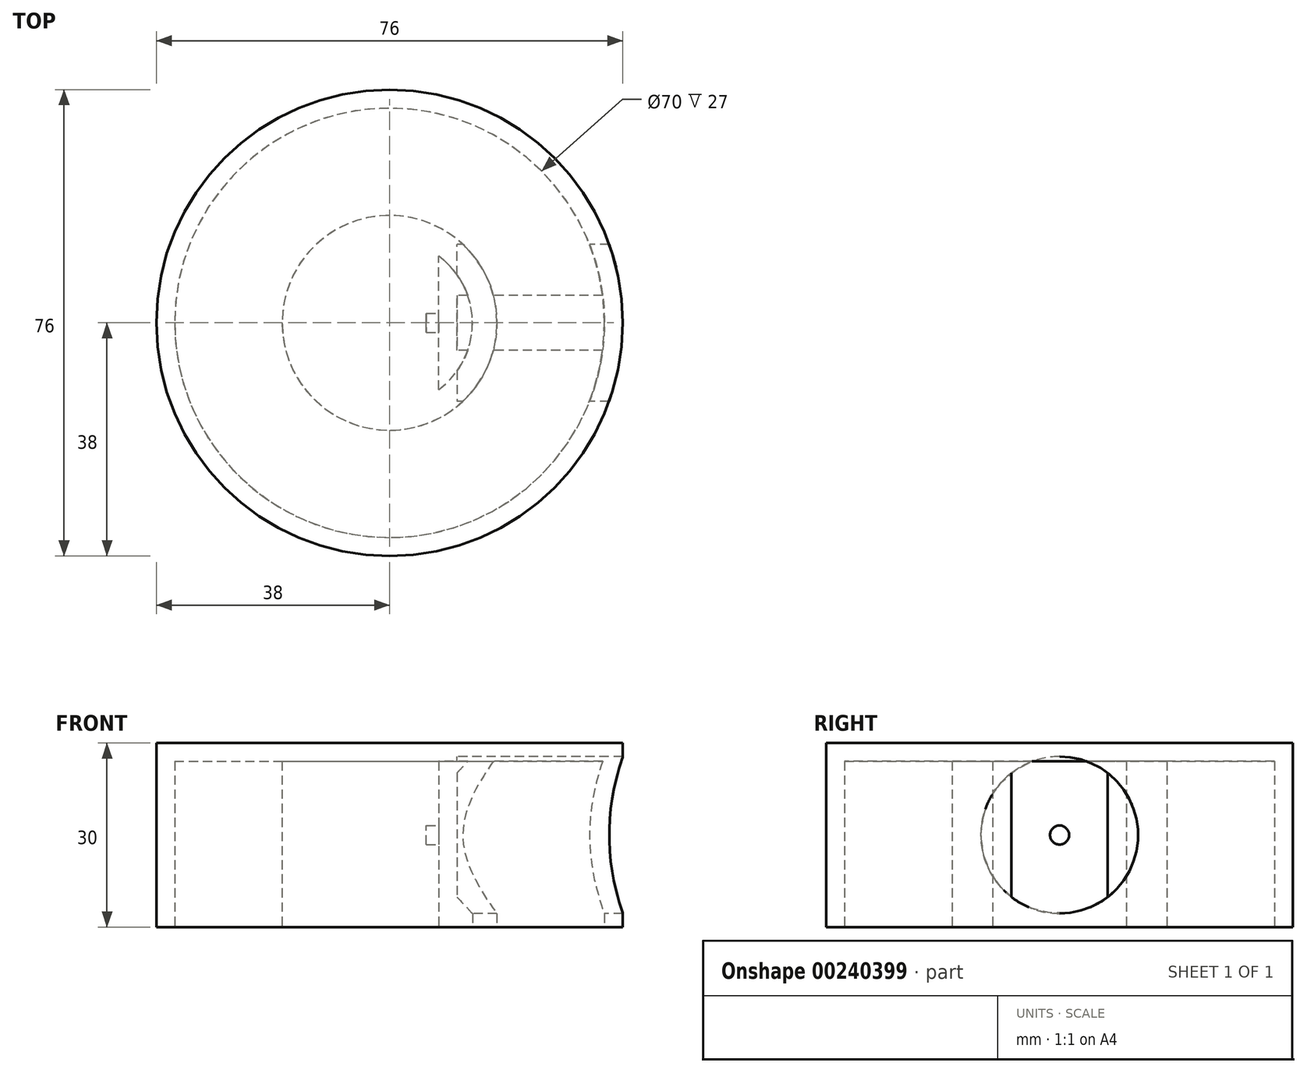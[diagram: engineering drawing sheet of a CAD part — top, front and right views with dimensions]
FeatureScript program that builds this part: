
annotation { "Feature Type Name" : "Feature", "Feature Type Description" : "" }
export const myFeature = defineFeature(function(context is Context, id is Id, definition is map)
    precondition{}
    {
        {
            var Q0;
            Q0=qCreatedBy(makeId("Top.planeOp"),FACE);
            var sketch = newSketch(context, id + "F0", { "sketchPlane" : qUnion([Q0])});
            skCircle(sketch, "E0", {"center": v(0, 0) * mm, "radius": 38 * mm});
            skSolve(sketch);
        }
        {
            var Q0;
            Q0 = qSketchRegion(id + "F0", true);
            extrude(context, id + "F1", {"entities" : qUnion([Q0]), "depth" : 30 * mm});
        }
        {
            var Q0;
            Q0=makeQuery(id+"F1.opExtrude","CAP_FACE",FACE,{"disambiguationData":[OSD([sQuery(id+"F0.wireOp",EDGE,"E0")])],"isStart":true});
            var sketch = newSketch(context, id + "F2", { "sketchPlane" : qUnion([Q0])});
            skCircle(sketch, "E1", {"center": v(0, 0) * mm, "radius": 17.5 * mm});
            skCircle(sketch, "E2", {"center": v(0, 0) * mm, "radius": 35 * mm});
            skSolve(sketch);
        }
        {
            var Q0;
            Q0 = qSketchRegion(id + "F2", true);
            extrude(context, id + "F3", {"entities" : qUnion([Q0]), "operationType" : NewBodyOperationType.REMOVE, "oppositeDirection" : true, "depth" : 27 * mm});
        }
        {
            var Q0;
            Q0=qCreatedBy(makeId("Right.planeOp"),FACE);
            var sketch = newSketch(context, id + "F4", { "sketchPlane" : qUnion([Q0])});
            skCircle(sketch, "E3", {"center": v(0, 15) * mm, "radius": 12.8 * mm});
            skSolve(sketch);
        }
        {
            var Q0;
            Q0 = qSketchRegion(id + "F4", true);
            extrude(context, id + "F5", {"entities" : qUnion([Q0]), "operationType" : NewBodyOperationType.REMOVE, "depth" : 46 * mm, "hasSecondDirection" : true, "secondDirectionOppositeDirection" : false, "secondDirectionDepth" : 11 * mm});
        }
        {
            var Q0;
            Q0=makeQuery(id+"F3.boolean.opBoolean","SPLIT",FACE,{"disambiguationData":[TD([makeQuery(id+"F3.opExtrude","SWEPT_FACE",FACE,{"disambiguationData":[OSD([sQuery(id+"F2.wireOp",EDGE,"E1")])]})])],"derivedFrom":makeQuery(id+"F1.opExtrude","CAP_FACE",FACE,{"disambiguationData":[OSD([sQuery(id+"F0.wireOp",EDGE,"E0")])],"isStart":true})});
            var sketch = newSketch(context, id + "F6", { "sketchPlane" : qUnion([Q0])});
            skCircle(sketch, "E4.0", {"center": v(0, 0) * mm, "radius": 13.5 * mm});
            skLineSegment(sketch, "E5.0", {"start": v(8, 12.8) * mm, "end": v(8, -12.8) * mm});
            skSolve(sketch);
        }
        {
            var Q0;
            {var subQ0=sQuery(id+"F6.wireOp",EDGE,"E5.0");var subQ1=sQuery(id+"F6.wireOp",EDGE,"E4.0");var subQ2=makeQuery(id+"F6.imprint","INTERSECT",VERTEX,{"disambiguationData":[OD(0.0)],"derivedFrom":[subQ1,subQ0]});Q0=makeQuery(id+"F6.imprint","IMPRINT",FACE,{"disambiguationData":[TD([[makeQuery(id+"F6.imprint","IMPRINT",EDGE,{"disambiguationData":[TD([[subQ2,-1.0]])],"derivedFrom":subQ1}),1.0]])]});}
            extrude(context, id + "F7", {"entities" : qUnion([Q0]), "operationType" : NewBodyOperationType.REMOVE, "oppositeDirection" : true, "depth" : 27 * mm});
        }
        {
            var Q0;
            Q0=makeQuery(id+"F5.boolean.opBoolean","COPY",FACE,{"derivedFrom":makeQuery(id+"F5.opExtrude","CAP_FACE",FACE,{"disambiguationData":[OSD([sQuery(id+"F4.wireOp",EDGE,"E3")])],"isStart":true})});
            var sketch = newSketch(context, id + "F8", { "sketchPlane" : qUnion([Q0])});
            skCircle(sketch, "E6", {"center": v(0, 15) * mm, "radius": 1.55 * mm});
            skSolve(sketch);
        }
        {
            var Q0;
            Q0 = qSketchRegion(id + "F8", true);
            extrude(context, id + "F9", {"entities" : qUnion([Q0]), "operationType" : NewBodyOperationType.REMOVE, "oppositeDirection" : true, "depth" : 5 * mm});
        }
    });
